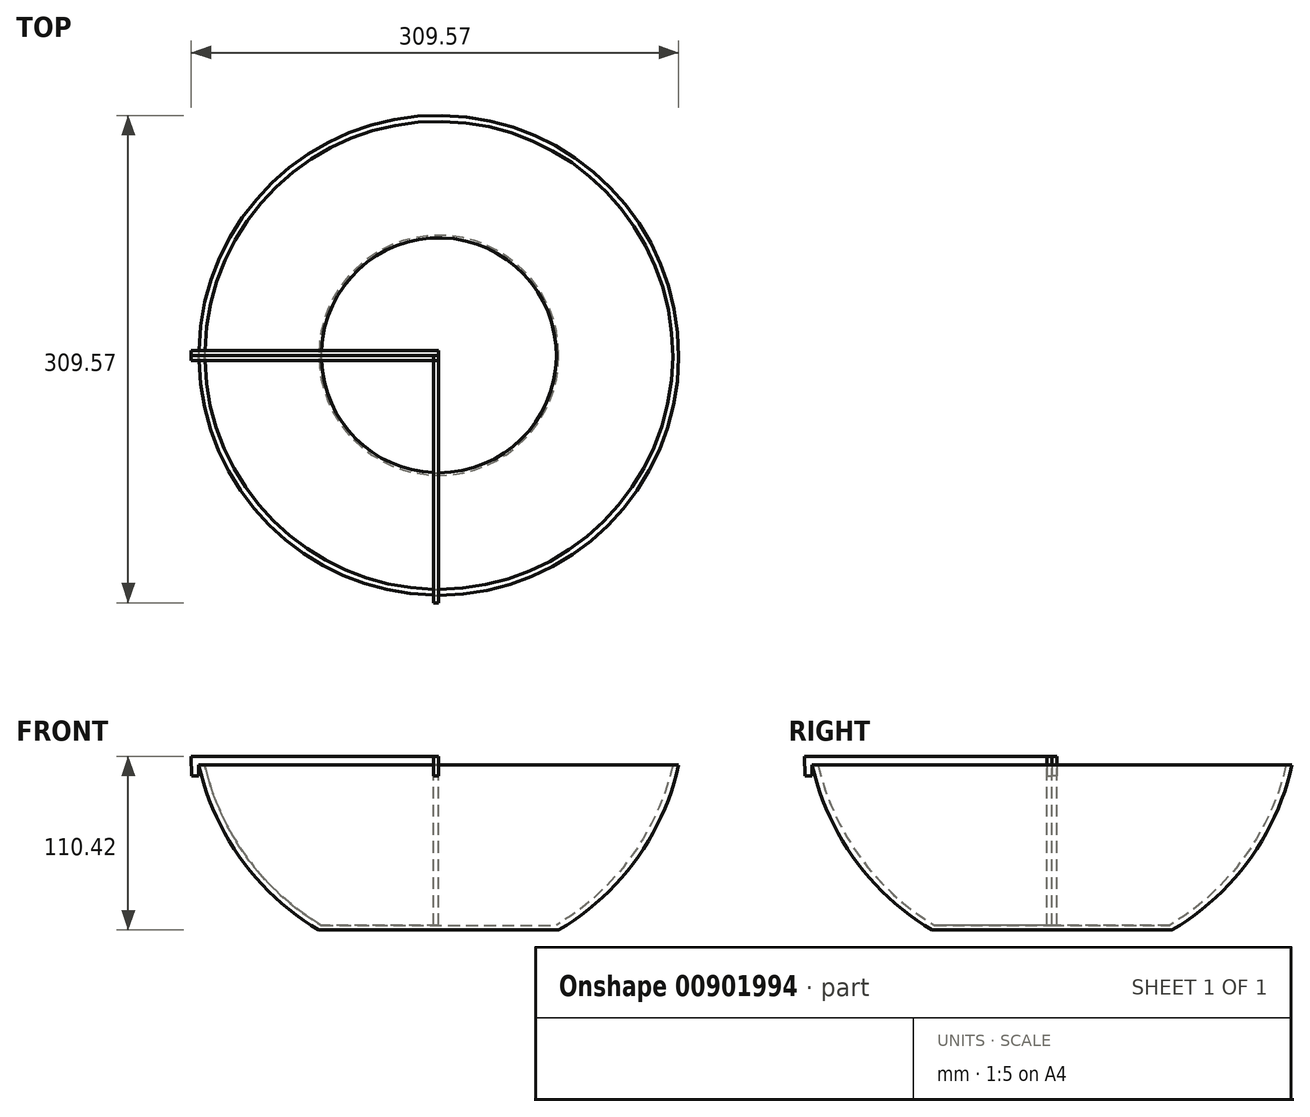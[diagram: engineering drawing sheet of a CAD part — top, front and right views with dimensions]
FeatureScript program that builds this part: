
annotation { "Feature Type Name" : "Feature", "Feature Type Description" : "" }
export const myFeature = defineFeature(function(context is Context, id is Id, definition is map)
    precondition{}
    {
        {
            var Q0;
            Q0=qCreatedBy(makeId("Front.planeOp"),FACE);
            var sketch = newSketch(context, id + "F0", { "sketchPlane" : qUnion([Q0])});
            skLineSegment(sketch, "E0", {"start": v(0, 0) * mm, "end": v(0, 104.78) * mm, "construction": true});
            skLineSegment(sketch, "E1", {"start": v(0, 0) * mm, "end": v(76.2, 0) * mm});
            skLineSegment(sketch, "E2.1", {"start": v(0, 3.07) * mm, "end": v(74.63, 3.07) * mm});
            skLineSegment(sketch, "E3", {"start": v(148.6, 104.78) * mm, "end": v(152.4, 104.78) * mm});
            skLineSegment(sketch, "E4", {"start": v(0, 3.07) * mm, "end": v(0, 0) * mm});
            skArc(sketch, "E5", {"start": v(76.2, 0) * mm, "mid": v(125.14, 44.5) * mm, "end": v(152.4, 104.78) * mm});
            skArc(sketch, "E6", {"start": v(74.63, 3.07) * mm, "mid": v(122.02, 46.36) * mm, "end": v(148.6, 104.78) * mm});
            skLineSegment(sketch, "E7", {"start": v(0, 104.78) * mm, "end": v(0, 3.07) * mm});
            skLineSegment(sketch, "E8.top", {"start": v(0, 110.42) * mm, "end": v(157.17, 110.42) * mm});
            skLineSegment(sketch, "E8.left", {"start": v(0, 104.78) * mm, "end": v(0, 110.42) * mm});
            skLineSegment(sketch, "E9.top", {"start": v(152.4, 97.98) * mm, "end": v(157.1, 97.98) * mm});
            skLineSegment(sketch, "E9.left", {"start": v(152.4, 104.78) * mm, "end": v(152.4, 97.98) * mm});
            skLineSegment(sketch, "E10.MirrorCS", {"start": v(0, 110.42) * mm, "end": v(-157.17, 110.42) * mm});
            skLineSegment(sketch, "E11.MirrorCS", {"start": v(-152.4, 97.98) * mm, "end": v(-157.1, 97.98) * mm});
            skArc(sketch, "E12.MirrorCS", {"start": v(-74.63, 3.07) * mm, "mid": v(-122.02, 46.36) * mm, "end": v(-148.6, 104.78) * mm});
            skLineSegment(sketch, "E13.MirrorCS", {"start": v(-148.6, 104.78) * mm, "end": v(-152.4, 104.78) * mm});
            skLineSegment(sketch, "E14.MirrorCS", {"start": v(0, 3.07) * mm, "end": v(-74.63, 3.07) * mm});
            skLineSegment(sketch, "E15.MirrorCS", {"start": v(-152.4, 104.78) * mm, "end": v(-152.4, 97.98) * mm});
            skPoint(sketch, "E16.trimOffspring.end.orphan", {"position": v(157.17, 104.78) * mm});
            skPoint(sketch, "E16.trimOffspring.start.orphan", {"position": v(157.1, 104.78) * mm});
            skLineSegment(sketch, "E17", {"start": v(157.17, 110.42) * mm, "end": v(157.1, 97.98) * mm});
            skPoint(sketch, "E18.MirrorCS.end.orphan", {"position": v(-157.1, 97.98) * mm});
            skPoint(sketch, "E18.MirrorCS.start.orphan", {"position": v(-157.1, 104.78) * mm});
            skPoint(sketch, "E19.MirrorCS.end.orphan", {"position": v(-157.17, 110.42) * mm});
            skPoint(sketch, "E19.MirrorCS.start.orphan", {"position": v(-157.17, 104.78) * mm});
            skLineSegment(sketch, "E20", {"start": v(-157.17, 110.42) * mm, "end": v(-157.1, 97.98) * mm});
            skSolve(sketch);
        }
        {
            var Q0;
            Q0=makeQuery(id+"F0.imprint","IMPRINT",FACE,{"disambiguationData":[TD([[makeQuery(id+"F0.imprint","IMPRINT",EDGE,{"derivedFrom":sQuery(id+"F0.wireOp",EDGE,"E1")}),1.0]])]});
            var Q1;
            Q1=sQuery(id+"F0.wireOp",EDGE,"E0");
            revolve(context, id + "F1", {"surfaceOperationType" : NewSurfaceOperationType.NEW, "entities" : qUnion([Q0]), "axis" : qUnion([Q1]), "revolveType" : RevolveType.FULL});
        }
        {
            var Q0;
            Q0=makeQuery(id+"F0.imprint","IMPRINT",FACE,{"disambiguationData":[TD([[makeQuery(id+"F0.imprint","IMPRINT",EDGE,{"derivedFrom":sQuery(id+"F0.wireOp",EDGE,"E2.1")}),1.0]])]});
            extrude(context, id + "F2", {"entities" : qUnion([Q0]), "depth" : 3.17 * mm, "offsetDistance" : 25.4 * mm});
        }
        {
            var Q0;
            Q0=makeQuery(id+"F2.opExtrude","SWEPT_BODY",BODY,{"disambiguationData":[OSD([sQuery(id+"F0.wireOp",EDGE,"E2.1"),sQuery(id+"F0.wireOp",EDGE,"E6"),sQuery(id+"F0.wireOp",EDGE,"E7"),sQuery(id+"F0.wireOp",EDGE,"E3"),sQuery(id+"F0.wireOp",EDGE,"E8.top"),sQuery(id+"F0.wireOp",EDGE,"E8.left"),sQuery(id+"F0.wireOp",EDGE,"E8.right"),sQuery(id+"F0.wireOp",EDGE,"E9.top"),sQuery(id+"F0.wireOp",EDGE,"E9.left"),sQuery(id+"F0.wireOp",EDGE,"E9.right"),sQuery(id+"F0.wireOp",EDGE,"E16.trimOffspring")])]});
            var Q1;
            Q1=makeQuery(id+"F2.opExtrude","SWEPT_FACE",FACE,{"disambiguationData":[OSD([sQuery(id+"F0.wireOp",EDGE,"E7"),sQuery(id+"F0.wireOp",EDGE,"E8.left")])]});
            mirror(context, id + "F3", {"entities" : qUnion([Q0]), "mirrorPlane" : qUnion([Q1])});
        }
        {
            var Q0;
            Q0=makeQuery(id+"F2.opExtrude","SWEPT_BODY",BODY,{"disambiguationData":[OSD([sQuery(id+"F0.wireOp",EDGE,"E2.1"),sQuery(id+"F0.wireOp",EDGE,"E6"),sQuery(id+"F0.wireOp",EDGE,"E7"),sQuery(id+"F0.wireOp",EDGE,"E3"),sQuery(id+"F0.wireOp",EDGE,"E8.top"),sQuery(id+"F0.wireOp",EDGE,"E8.left"),sQuery(id+"F0.wireOp",EDGE,"E9.top"),sQuery(id+"F0.wireOp",EDGE,"E9.left"),sQuery(id+"F0.wireOp",EDGE,"E17")])]});
            var Q1;
            Q1=sQuery(id+"F0.wireOp",EDGE,"E7");
            circularPattern(context, id + "F4", {"entities" : qUnion([Q0]), "axis" : qUnion([Q1]), "angle" : 360 * degree, "instanceCount" : 4, "equalSpace" : true});
        }
        {
            var Q0;
            Q0=makeQuery(id+"F4.opPattern","COPY",BODY,{"derivedFrom":makeQuery(id+"F2.opExtrude","SWEPT_BODY",BODY,{"disambiguationData":[OSD([sQuery(id+"F0.wireOp",EDGE,"E2.1"),sQuery(id+"F0.wireOp",EDGE,"E6"),sQuery(id+"F0.wireOp",EDGE,"E7"),sQuery(id+"F0.wireOp",EDGE,"E3"),sQuery(id+"F0.wireOp",EDGE,"E8.top"),sQuery(id+"F0.wireOp",EDGE,"E8.left"),sQuery(id+"F0.wireOp",EDGE,"E9.top"),sQuery(id+"F0.wireOp",EDGE,"E9.left"),sQuery(id+"F0.wireOp",EDGE,"E17")])]}),"instanceName":"3"});
            deleteBodies(context, id + "F5", {"entities" : qUnion([Q0])});
        }
        {
            var Q0;
            Q0=makeQuery(id+"F2.opExtrude","SWEPT_BODY",BODY,{"disambiguationData":[OSD([sQuery(id+"F0.wireOp",EDGE,"E2.1"),sQuery(id+"F0.wireOp",EDGE,"E6"),sQuery(id+"F0.wireOp",EDGE,"E7"),sQuery(id+"F0.wireOp",EDGE,"E3"),sQuery(id+"F0.wireOp",EDGE,"E8.top"),sQuery(id+"F0.wireOp",EDGE,"E8.left"),sQuery(id+"F0.wireOp",EDGE,"E9.top"),sQuery(id+"F0.wireOp",EDGE,"E9.left"),sQuery(id+"F0.wireOp",EDGE,"E17")])]});
            deleteBodies(context, id + "F6", {"entities" : qUnion([Q0])});
        }
    });
